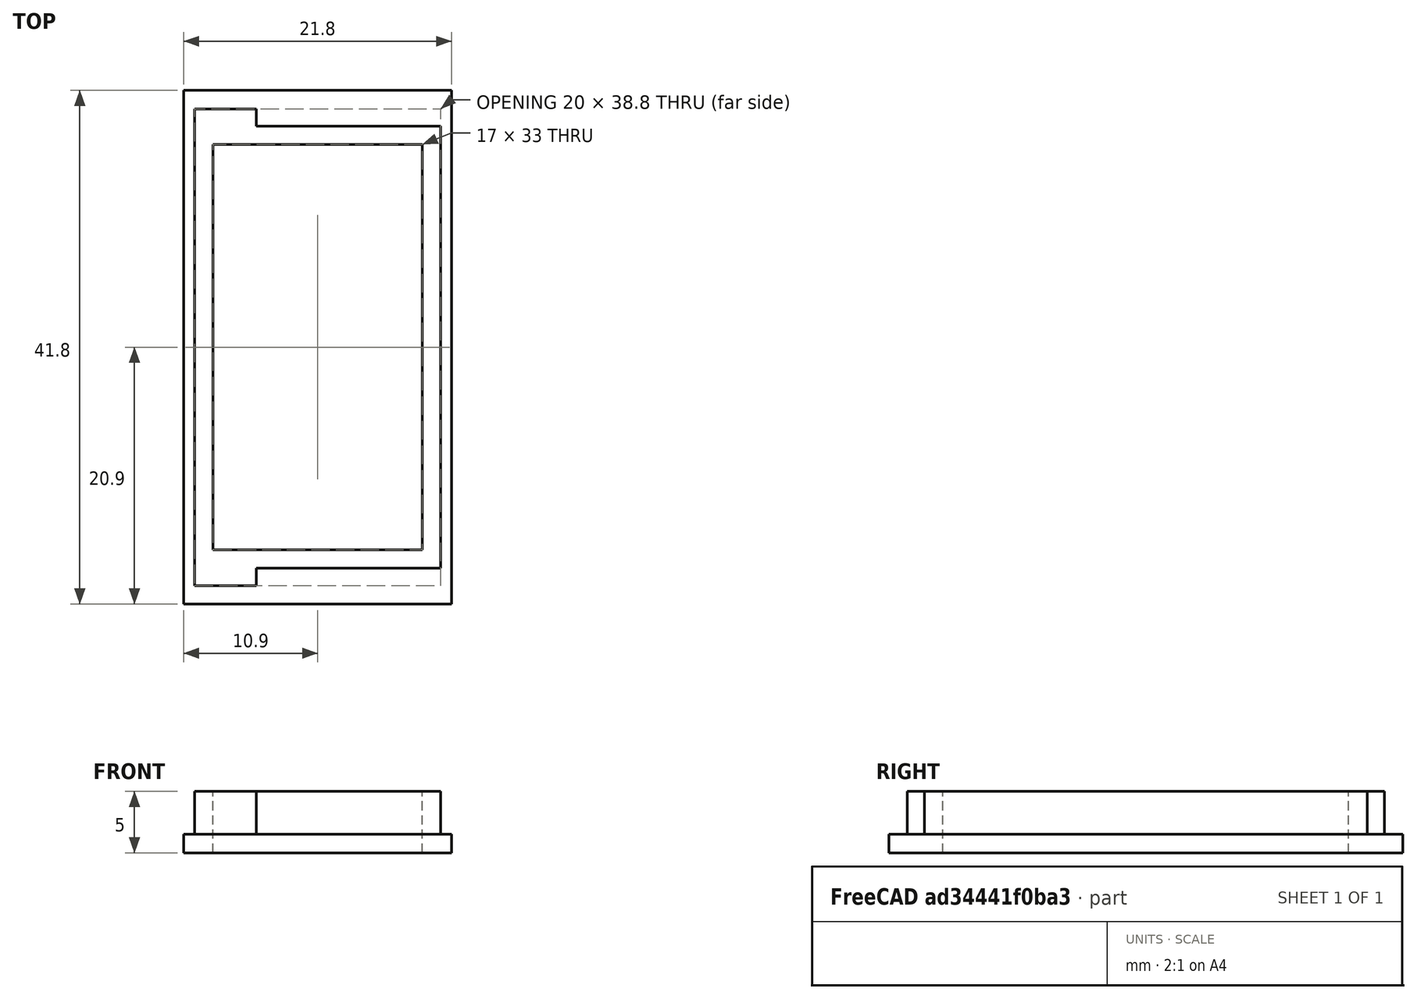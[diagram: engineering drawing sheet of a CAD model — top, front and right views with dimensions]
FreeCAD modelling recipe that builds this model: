
FCSTD DOCUMENT  (FreeCAD 0.17R13522 (Git))
Label: BaseLowerSensorMount
License: All rights reserved
LicenseURL: http://en.wikipedia.org/wiki/All_rights_reserved
objects: Part::Box×5, Part::MultiFuse×3, Part::Cut×1
note: 9 computed .brp shape members not serialized (recipe doc carries the construction recipe); baked Part::Feature solids carry a one-line shape summary decoded from their .brp

FEATURE [Part::Box] Box064  label="Cube062"
  AttacherType = Attacher::AttachEngine3D
  Height = 5
  Length = 5
  Placement = pos=(-10,17.4,0) rot=(0,0,1;0rad)
  Width = 2
FEATURE [Part::Box] Box065  label="Cube063"
  AttacherType = Attacher::AttachEngine3D
  Height = 5
  Length = 20
  Placement = pos=(-10,-18,0) rot=(0,0,1;0rad)
  Width = 36
FEATURE [Part::Box] Box066  label="cut001"
  AttacherType = Attacher::AttachEngine3D
  Height = 5
  Length = 17
  Placement = pos=(-8.5,-16.5,0) rot=(0,0,1;0rad)
  Width = 33
FEATURE [Part::Box] Box067  label="Cube064"
  AttacherType = Attacher::AttachEngine3D
  Height = 5
  Length = 5
  Placement = pos=(-10,-19.4,0) rot=(0,0,1;0rad)
  Width = 2
FEATURE [Part::MultiFuse] Fusion018
  Shapes = -> [Box067,Box064]
FEATURE [Part::Box] Box068  label="outer base001"
  AttacherType = Attacher::AttachEngine3D
  Height = 1.5
  Length = 21.8
  Placement = pos=(-10.9,-20.9,0) rot=(0,0,1;0rad)
  Width = 41.8
FEATURE [Part::MultiFuse] Fusion016
  Shapes = -> [Box068,Box065]
FEATURE [Part::Cut] Cut059  label="Base001"
  Base = -> Fusion016
  Tool = -> Box066
FEATURE [Part::MultiFuse] Fusion017  label="BaseSensorLowerMount"
  Placement = pos=(0,0,141.7) rot=(0,1,0;0rad)
  Shapes = -> [Cut059,Fusion018]
